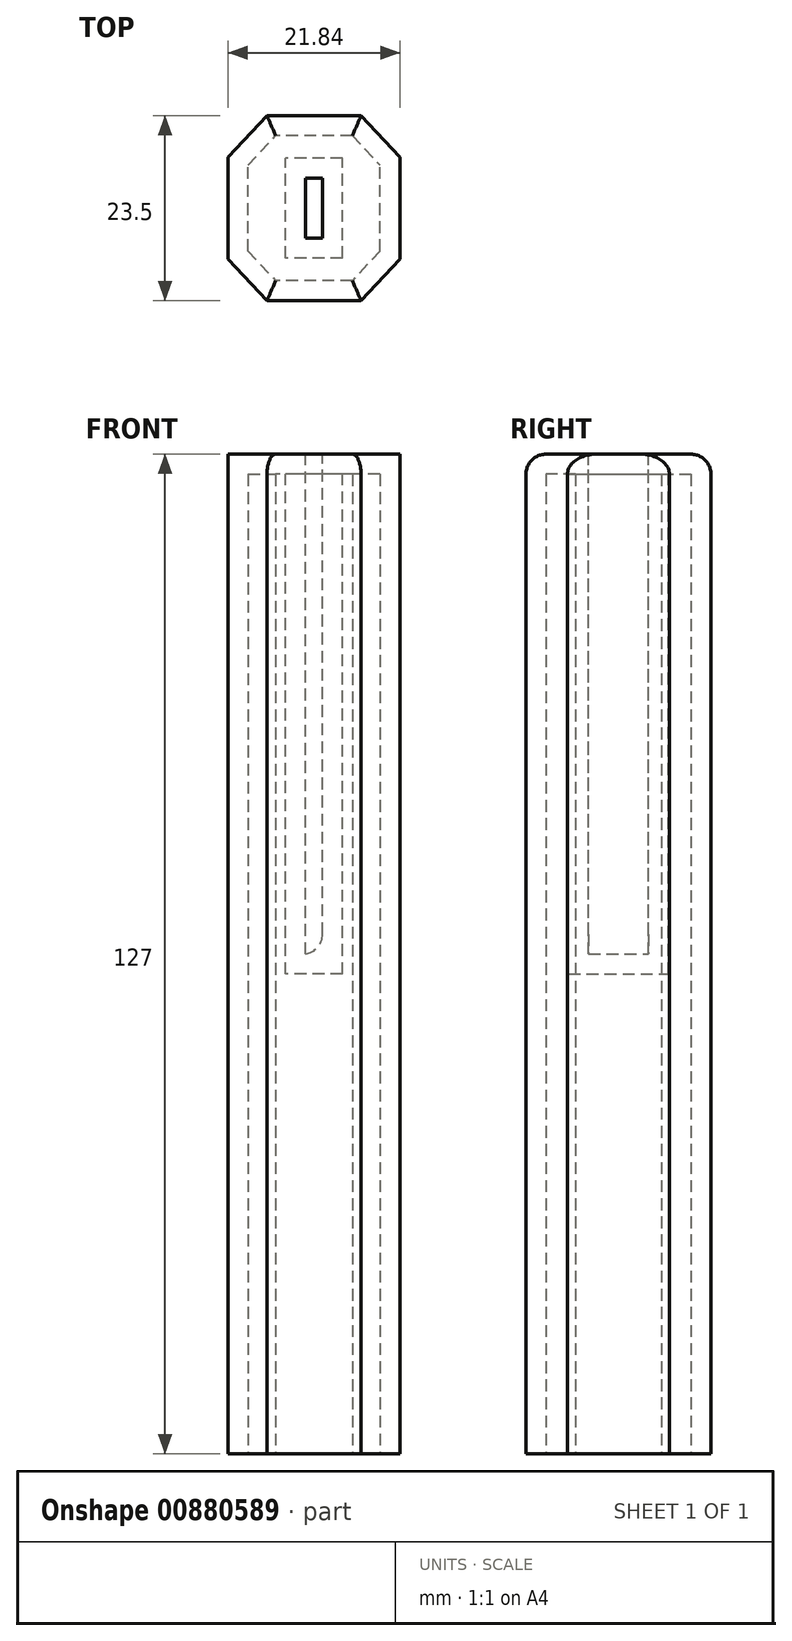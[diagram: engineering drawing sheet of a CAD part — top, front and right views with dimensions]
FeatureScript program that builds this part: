
annotation { "Feature Type Name" : "Feature", "Feature Type Description" : "" }
export const myFeature = defineFeature(function(context is Context, id is Id, definition is map)
    precondition{}
    {
        {
            var Q0;
            Q0=qCreatedBy(makeId("Top.planeOp"),FACE);
            var sketch = newSketch(context, id + "F0", { "sketchPlane" : qUnion([Q0])});
            skLineSegment(sketch, "E0.bottom", {"start": v(5.97, -11.75) * mm, "end": v(-5.97, -11.75) * mm});
            skLineSegment(sketch, "E0.top", {"start": v(5.97, 11.75) * mm, "end": v(-5.97, 11.75) * mm});
            skLineSegment(sketch, "E0.left", {"start": v(10.92, -6.48) * mm, "end": v(10.92, 6.48) * mm});
            skLineSegment(sketch, "E0.right", {"start": v(-10.92, -6.48) * mm, "end": v(-10.92, 6.48) * mm});
            skPoint(sketch, "E0.middle", {"position": v(0, 0) * mm});
            skLineSegment(sketch, "E1.left", {"start": v(10.92, 6.48) * mm, "end": v(10.92, -6.48) * mm});
            skLineSegment(sketch, "E1.right", {"start": v(-10.92, 6.48) * mm, "end": v(-10.92, -6.48) * mm});
            skLineSegment(sketch, "E2", {"start": v(5.97, 11.75) * mm, "end": v(10.92, 6.48) * mm});
            skLineSegment(sketch, "E3", {"start": v(10.92, -6.48) * mm, "end": v(5.97, -11.75) * mm});
            skLineSegment(sketch, "E4", {"start": v(-10.92, -6.48) * mm, "end": v(-5.97, -11.75) * mm});
            skLineSegment(sketch, "E5", {"start": v(-10.92, 6.48) * mm, "end": v(-5.97, 11.75) * mm});
            skSolve(sketch);
        }
        {
            var Q0;
            Q0=makeQuery(id+"F0.imprint","IMPRINT",FACE,{"disambiguationData":[TD([[makeQuery(id+"F0.imprint","IMPRINT",EDGE,{"derivedFrom":sQuery(id+"F0.wireOp",EDGE,"E0.top")}),1.0]])]});
            extrude(context, id + "F1", {"entities" : qUnion([Q0]), "depth" : 127 * mm});
        }
        {
            var Q0;
            Q0=makeQuery(id+"F1.opExtrude","CAP_FACE",FACE,{"disambiguationData":[OSD([sQuery(id+"F0.wireOp",EDGE,"E0.top"),sQuery(id+"F0.wireOp",EDGE,"E0.bottom"),sQuery(id+"F0.wireOp",EDGE,"E1.left"),sQuery(id+"F0.wireOp",EDGE,"E1.right"),sQuery(id+"F0.wireOp",EDGE,"E2"),sQuery(id+"F0.wireOp",EDGE,"E3"),sQuery(id+"F0.wireOp",EDGE,"E4"),sQuery(id+"F0.wireOp",EDGE,"E5")])],"isStart":false});
            var sketch = newSketch(context, id + "F2", { "sketchPlane" : qUnion([Q0])});
            skLineSegment(sketch, "E6.bottom", {"start": v(1.08, -3.81) * mm, "end": v(-1.08, -3.81) * mm});
            skLineSegment(sketch, "E6.top", {"start": v(1.08, 3.81) * mm, "end": v(-1.08, 3.81) * mm});
            skLineSegment(sketch, "E6.left", {"start": v(1.08, -3.8) * mm, "end": v(1.08, 3.81) * mm});
            skLineSegment(sketch, "E6.right", {"start": v(-1.08, -3.81) * mm, "end": v(-1.08, 3.81) * mm});
            skPoint(sketch, "E6.middle", {"position": v(0, 0) * mm});
            skSolve(sketch);
        }
        {
            var Q0;
            Q0=makeQuery(id+"F2.imprint","IMPRINT",FACE,{"disambiguationData":[TD([[makeQuery(id+"F2.imprint","IMPRINT",EDGE,{"derivedFrom":sQuery(id+"F2.wireOp",EDGE,"E6.bottom")}),-1.0]])]});
            extrude(context, id + "F3", {"entities" : qUnion([Q0]), "operationType" : NewBodyOperationType.REMOVE, "oppositeDirection" : true, "depth" : 63.5 * mm});
        }
        {
            var Q0;
            Q0=makeQuery(id+"F1.opExtrude","CAP_FACE",FACE,{"disambiguationData":[OSD([sQuery(id+"F0.wireOp",EDGE,"E0.top"),sQuery(id+"F0.wireOp",EDGE,"E0.bottom"),sQuery(id+"F0.wireOp",EDGE,"E1.left"),sQuery(id+"F0.wireOp",EDGE,"E1.right"),sQuery(id+"F0.wireOp",EDGE,"E2"),sQuery(id+"F0.wireOp",EDGE,"E3"),sQuery(id+"F0.wireOp",EDGE,"E4"),sQuery(id+"F0.wireOp",EDGE,"E5")])],"isStart":true});
            shell(context, id + "F4", {"entities" : qUnion([Q0]), "thickness" : 2.54 * mm});
        }
        {
            var Q0;
            Q0=makeQuery(id+"F1.opExtrude","CAP_EDGE",EDGE,{"disambiguationData":[OSD([sQuery(id+"F0.wireOp",EDGE,"E1.left")])],"isStart":false});
            var Q1;
            Q1=makeQuery(id+"F1.opExtrude","CAP_EDGE",EDGE,{"disambiguationData":[OSD([sQuery(id+"F0.wireOp",EDGE,"E0.top")])],"isStart":false});
            var Q2;
            Q2=makeQuery(id+"F1.opExtrude","CAP_EDGE",EDGE,{"disambiguationData":[OSD([sQuery(id+"F0.wireOp",EDGE,"E1.right")])],"isStart":false});
            var Q3;
            Q3=makeQuery(id+"F1.opExtrude","CAP_EDGE",EDGE,{"disambiguationData":[OSD([sQuery(id+"F0.wireOp",EDGE,"E0.bottom")])],"isStart":false});
            var Q4;
            Q4=makeQuery(id+"F1.opExtrude","CAP_EDGE",EDGE,{"disambiguationData":[OSD([sQuery(id+"F0.wireOp",EDGE,"E5")])],"isStart":false});
            var Q5;
            Q5=makeQuery(id+"F1.opExtrude","CAP_EDGE",EDGE,{"disambiguationData":[OSD([sQuery(id+"F0.wireOp",EDGE,"E2")])],"isStart":false});
            var Q6;
            Q6=makeQuery(id+"F1.opExtrude","CAP_EDGE",EDGE,{"disambiguationData":[OSD([sQuery(id+"F0.wireOp",EDGE,"E3")])],"isStart":false});
            var Q7;
            Q7=makeQuery(id+"F1.opExtrude","CAP_EDGE",EDGE,{"disambiguationData":[OSD([sQuery(id+"F0.wireOp",EDGE,"E4")])],"isStart":false});
            fillet(context, id + "F5", {"entities" : qUnion([Q0, Q1, Q2, Q3, Q4, Q5, Q6, Q7]), "radius" : 2.54 * mm, "tangentPropagation" : true, "allowEdgeOverflow" : false});
        }
        {
            var Q0;
            Q0=makeQuery(id+"F3.boolean.opBoolean","COPY",EDGE,{"derivedFrom":makeQuery(id+"F3.opExtrude","CAP_EDGE",EDGE,{"disambiguationData":[OSD([sQuery(id+"F2.wireOp",EDGE,"E6.left")])],"isStart":false})});
            fillet(context, id + "F6", {"entities" : qUnion([Q0]), "radius" : 2.54 * mm, "tangentPropagation" : true, "allowEdgeOverflow" : false});
        }
    });
